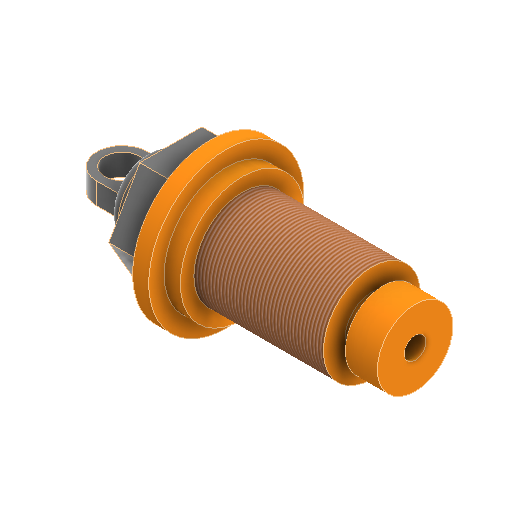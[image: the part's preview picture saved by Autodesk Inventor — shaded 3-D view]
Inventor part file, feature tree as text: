
AUTODESK INVENTOR PART (.ipt)
format: ipt  version: 2025 (Build 290162000, 162)  size: 262,656 bytes
history: native  units: in
note: dims shown in document units (in); Inventor stores cm internally (conversion verified against a paired STEP export)
features: sketch x3, extrude x2, revolve x1, fillet x1, thread x1, projected_geometry x1
ambient origin geometry x8: Origin, YZ Plane, XZ Plane, XY Plane, X Axis, Y Axis, Z Axis, Center Point
bodies: Solid1 (feature_tree)
feature tree (9):
  revolve  "Revolution1"  [1 undecoded]
  extrude  "Extrusion1"  Depth=0.0787in
  fillet  "Fillet1"  Radius=0.1969in
  extrude  "Extrusion2"  Depth=0.0787in
  thread  "Thread1"  [1 undecoded]
  sketch  "Sketch1"  dims[d0=1.9685in d1=0.2756in]
  sketch  "Sketch2"  dims[d2=0.2362in d3=0.0787in d4=0.1969in]
  projected_geometry  "Projected Loop1"
  sketch  "Sketch3"  dims[d6=0.9449in d7=0.1181in d8=0.1181in d9=0.4528in d10=0.3543in d11=360.0deg d12=0.0787in d13=0.2559in d14=0.1575in d15=0.0in d16=0.0787in d17=0.1575in d18=0.0in d19=0.945in d20=0.0in]
note: 2 required parameter values undecoded (feature->parameter linkage not recoverable at this tier; creation-order binding heuristic only, values carry confidence <= 0.55)